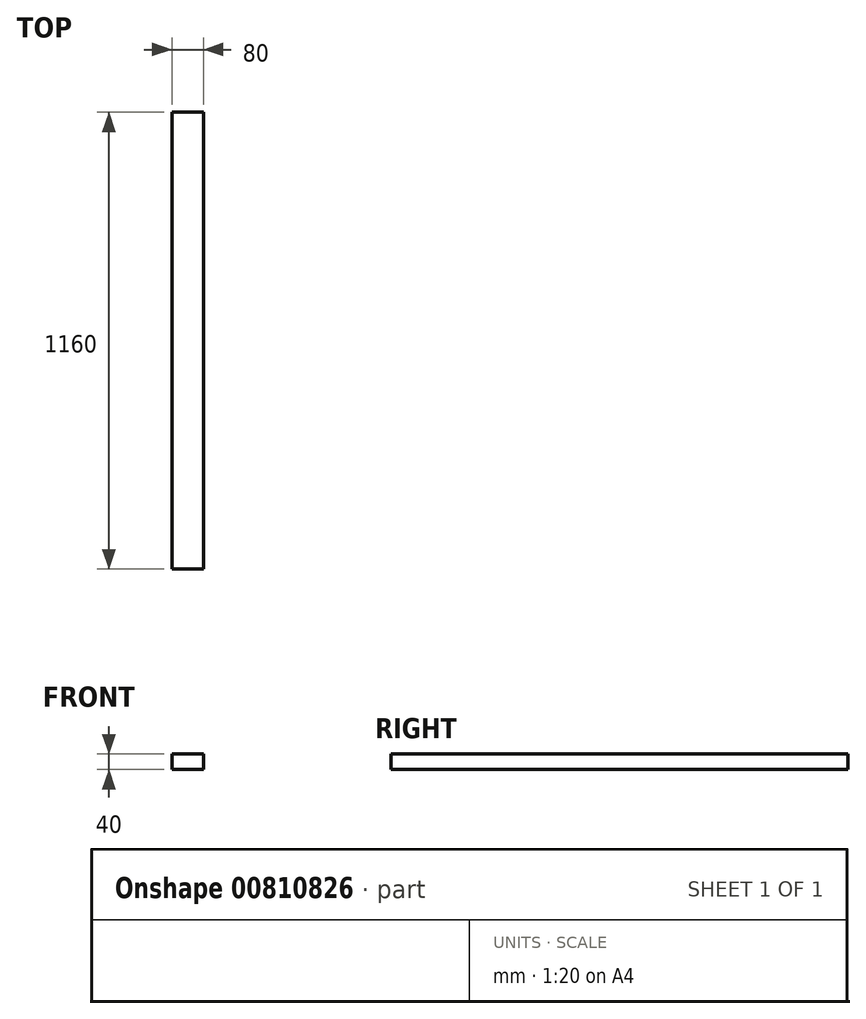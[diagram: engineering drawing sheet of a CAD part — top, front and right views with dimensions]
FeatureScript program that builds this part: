
annotation { "Feature Type Name" : "Feature", "Feature Type Description" : "" }
export const myFeature = defineFeature(function(context is Context, id is Id, definition is map)
    precondition{}
    {
        {
            var Q0;
            Q0=qCreatedBy(makeId("Front.planeOp"),FACE);
            var sketch = newSketch(context, id + "F0", { "sketchPlane" : qUnion([Q0])});
            skLineSegment(sketch, "E0.bottom", {"start": v(40, 20) * mm, "end": v(-40, 20) * mm});
            skLineSegment(sketch, "E0.top", {"start": v(40, -20) * mm, "end": v(-40, -20) * mm});
            skLineSegment(sketch, "E0.left", {"start": v(40, 20) * mm, "end": v(40, -20) * mm});
            skLineSegment(sketch, "E0.right", {"start": v(-40, 20) * mm, "end": v(-40, -20) * mm});
            skPoint(sketch, "E0.middle", {"position": v(0, 0) * mm});
            skSolve(sketch);
        }
        {
            var Q0;
            Q0=makeQuery(id+"F0.imprint","IMPRINT",FACE,{"disambiguationData":[TD([[makeQuery(id+"F0.imprint","IMPRINT",EDGE,{"derivedFrom":sQuery(id+"F0.wireOp",EDGE,"E0.bottom")}),1.0]])]});
            extrude(context, id + "F1", {"entities" : qUnion([Q0]), "endBound" : BoundingType.SYMMETRIC, "depth" : 1160 * mm, "offsetDistance" : 25 * mm});
        }
    });
